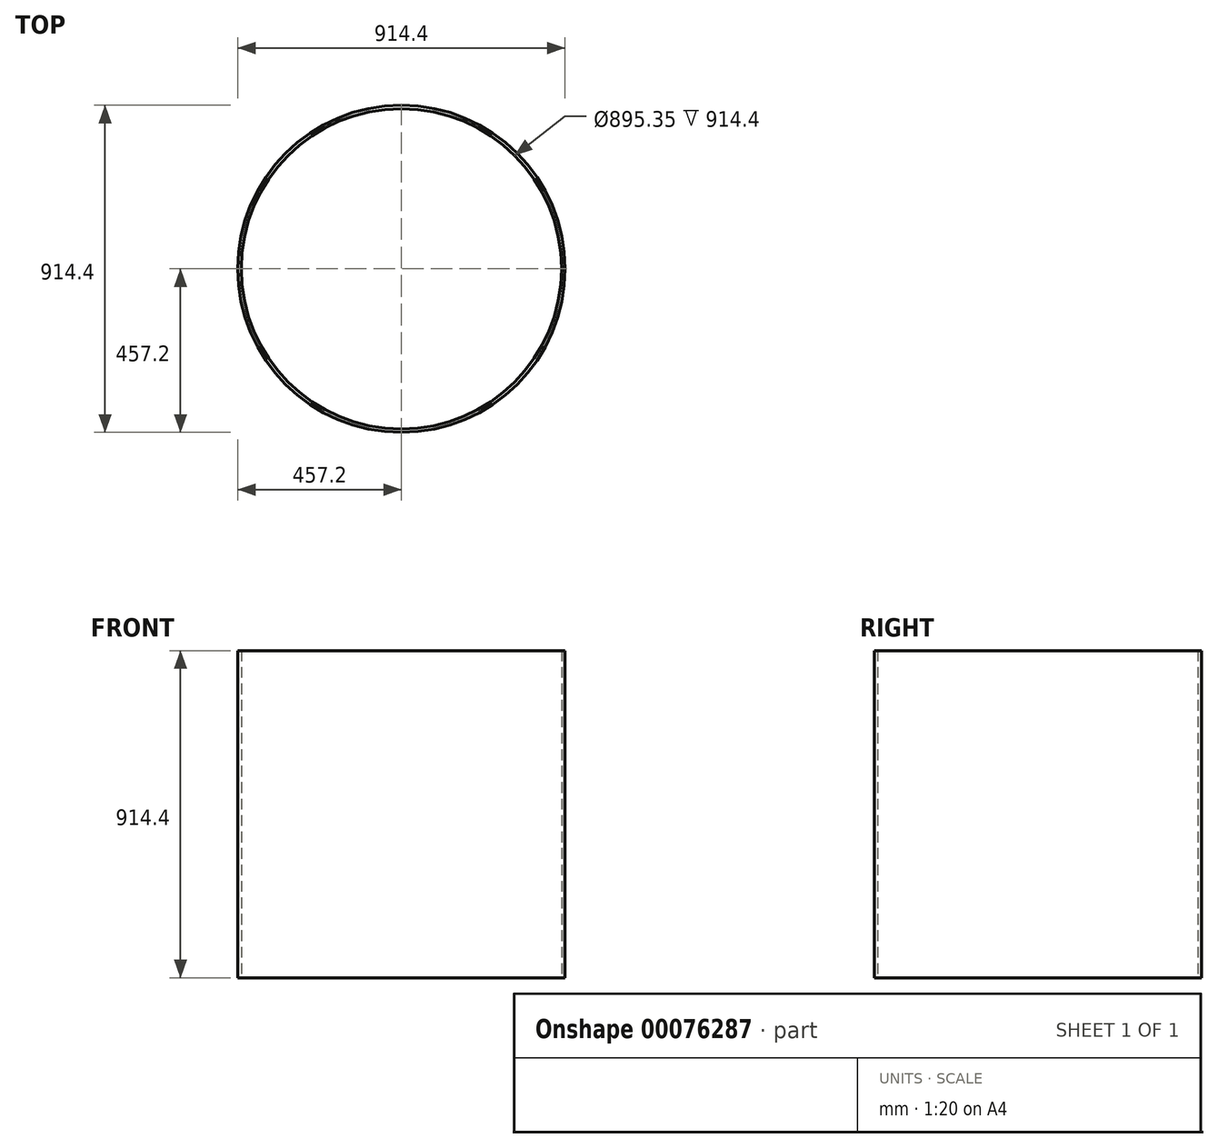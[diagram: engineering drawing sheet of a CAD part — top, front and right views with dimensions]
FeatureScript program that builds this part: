
annotation { "Feature Type Name" : "Feature", "Feature Type Description" : "" }
export const myFeature = defineFeature(function(context is Context, id is Id, definition is map)
    precondition{}
    {
        {
            var Q0;
            Q0=qCreatedBy(makeId("Top.planeOp"),FACE);
            var sketch = newSketch(context, id + "F0", { "sketchPlane" : qUnion([Q0])});
            skCircle(sketch, "E0", {"center": v(0, 0) * mm, "radius": 457.2 * mm});
            skCircle(sketch, "E1", {"center": v(0, 0) * mm, "radius": 447.68 * mm});
            skSolve(sketch);
        }
        {
            var Q0;
            Q0=qSketchRegion(id+"F0",true);
            extrude(context, id + "F1", {"entities" : qUnion([Q0]), "depth" : 914.4 * mm});
        }
    });
